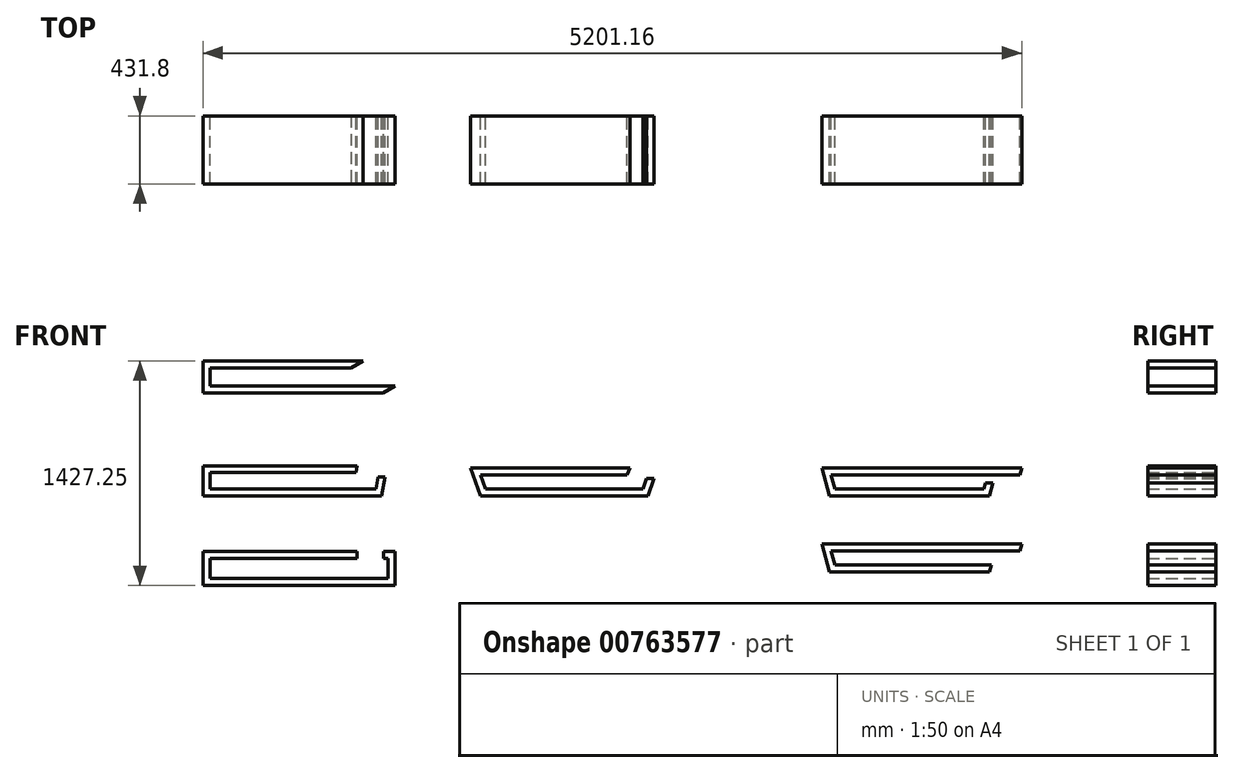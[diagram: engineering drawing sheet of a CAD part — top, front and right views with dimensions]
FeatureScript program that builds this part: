
annotation { "Feature Type Name" : "Feature", "Feature Type Description" : "" }
export const myFeature = defineFeature(function(context is Context, id is Id, definition is map)
    precondition{}
    {
        {
            var Q0;
            Q0=qCreatedBy(makeId("Front.planeOp"),FACE);
            var sketch = newSketch(context, id + "F0", { "sketchPlane" : qUnion([Q0])});
            skLineSegment(sketch, "E0", {"start": v(1016, 203.2) * mm, "end": v(0, 203.2) * mm});
            skLineSegment(sketch, "E1", {"start": v(0, 203.2) * mm, "end": v(0, 0) * mm});
            skLineSegment(sketch, "E2", {"start": v(0, 0) * mm, "end": v(1219.2, 0) * mm});
            skLineSegment(sketch, "E3", {"start": v(1219.2, 0) * mm, "end": v(1219.2, 44.45) * mm});
            skLineSegment(sketch, "E4", {"start": v(1219.2, 44.45) * mm, "end": v(44.45, 44.45) * mm});
            skLineSegment(sketch, "E5", {"start": v(44.45, 44.45) * mm, "end": v(44.45, 158.75) * mm});
            skLineSegment(sketch, "E6", {"start": v(44.45, 158.75) * mm, "end": v(1016, 158.75) * mm});
            skLineSegment(sketch, "E7", {"start": v(1016, 158.75) * mm, "end": v(1016, 203.2) * mm});
            skLineSegment(sketch, "E8", {"start": v(980.24, -462.8) * mm, "end": v(0, -462.8) * mm});
            skLineSegment(sketch, "E9", {"start": v(0, -462.8) * mm, "end": v(0, -653.3) * mm});
            skLineSegment(sketch, "E10", {"start": v(0, -653.3) * mm, "end": v(1136.08, -653.3) * mm});
            skLineSegment(sketch, "E11", {"start": v(1136.08, -653.3) * mm, "end": v(1157.46, -532.09) * mm});
            skLineSegment(sketch, "E12", {"start": v(1157.46, -532.09) * mm, "end": v(1112.32, -532.09) * mm});
            skLineSegment(sketch, "E13", {"start": v(1112.32, -532.09) * mm, "end": v(1098.78, -608.85) * mm});
            skLineSegment(sketch, "E14", {"start": v(1098.78, -608.85) * mm, "end": v(44.45, -608.85) * mm});
            skLineSegment(sketch, "E15", {"start": v(44.45, -608.85) * mm, "end": v(44.45, -506.58) * mm});
            skLineSegment(sketch, "E16", {"start": v(44.45, -506.58) * mm, "end": v(972.52, -506.58) * mm});
            skLineSegment(sketch, "E17", {"start": v(972.52, -506.58) * mm, "end": v(980.24, -462.8) * mm});
            skLineSegment(sketch, "E18", {"start": v(980.24, -1007.28) * mm, "end": v(0, -1007.28) * mm});
            skLineSegment(sketch, "E19", {"start": v(0, -1007.28) * mm, "end": v(0, -1224.05) * mm});
            skLineSegment(sketch, "E20", {"start": v(0, -1224.05) * mm, "end": v(1219.2, -1224.05) * mm});
            skLineSegment(sketch, "E21", {"start": v(1219.2, -1224.05) * mm, "end": v(1219.2, -1007.28) * mm});
            skLineSegment(sketch, "E22", {"start": v(1219.2, -1007.28) * mm, "end": v(1146.26, -1007.28) * mm});
            skLineSegment(sketch, "E23", {"start": v(1146.26, -1007.28) * mm, "end": v(1146.26, -1051.73) * mm});
            skLineSegment(sketch, "E24", {"start": v(1146.26, -1051.73) * mm, "end": v(1174.75, -1051.73) * mm});
            skLineSegment(sketch, "E25", {"start": v(1174.75, -1051.73) * mm, "end": v(1174.75, -1179.6) * mm});
            skLineSegment(sketch, "E26", {"start": v(1174.75, -1179.6) * mm, "end": v(44.45, -1179.6) * mm});
            skLineSegment(sketch, "E27", {"start": v(44.45, -1179.6) * mm, "end": v(44.45, -1051.73) * mm});
            skLineSegment(sketch, "E28", {"start": v(44.45, -1051.73) * mm, "end": v(980.24, -1051.73) * mm});
            skLineSegment(sketch, "E29", {"start": v(980.24, -1051.73) * mm, "end": v(980.24, -1007.28) * mm});
            skLineSegment(sketch, "E30", {"start": v(2711.3, -475.5) * mm, "end": v(1698.34, -475.5) * mm});
            skLineSegment(sketch, "E31", {"start": v(1698.34, -475.5) * mm, "end": v(1763.05, -653.3) * mm});
            skLineSegment(sketch, "E32", {"start": v(1763.05, -653.3) * mm, "end": v(2826.15, -653.3) * mm});
            skLineSegment(sketch, "E33", {"start": v(2826.15, -653.3) * mm, "end": v(2866.22, -543.22) * mm});
            skLineSegment(sketch, "E34", {"start": v(2866.22, -543.22) * mm, "end": v(2818.91, -543.22) * mm});
            skLineSegment(sketch, "E35", {"start": v(2818.91, -543.22) * mm, "end": v(2795.03, -608.85) * mm});
            skLineSegment(sketch, "E36", {"start": v(2795.03, -608.85) * mm, "end": v(1794.17, -608.85) * mm});
            skLineSegment(sketch, "E37", {"start": v(1794.17, -608.85) * mm, "end": v(1761.82, -519.95) * mm});
            skLineSegment(sketch, "E38", {"start": v(1761.82, -519.95) * mm, "end": v(2695.12, -519.95) * mm});
            skLineSegment(sketch, "E39", {"start": v(2695.12, -519.95) * mm, "end": v(2711.3, -475.5) * mm});
            skLineSegment(sketch, "E40", {"start": v(5201.16, -475.5) * mm, "end": v(3931.16, -475.5) * mm});
            skLineSegment(sketch, "E41", {"start": v(3931.16, -475.5) * mm, "end": v(3978.8, -653.3) * mm});
            skLineSegment(sketch, "E42", {"start": v(3978.8, -653.3) * mm, "end": v(4994.8, -653.3) * mm});
            skLineSegment(sketch, "E43", {"start": v(4994.8, -653.3) * mm, "end": v(5016.92, -570.75) * mm});
            skLineSegment(sketch, "E44", {"start": v(5016.92, -570.75) * mm, "end": v(4970.9, -570.75) * mm});
            skLineSegment(sketch, "E45", {"start": v(4970.9, -570.75) * mm, "end": v(4960.7, -608.85) * mm});
            skLineSegment(sketch, "E46", {"start": v(4960.7, -608.85) * mm, "end": v(4012.91, -608.85) * mm});
            skLineSegment(sketch, "E47", {"start": v(4012.91, -608.85) * mm, "end": v(3989.1, -519.95) * mm});
            skLineSegment(sketch, "E48", {"start": v(3989.1, -519.95) * mm, "end": v(5189.25, -519.95) * mm});
            skLineSegment(sketch, "E49", {"start": v(5189.25, -519.95) * mm, "end": v(5201.16, -475.5) * mm});
            skLineSegment(sketch, "E50", {"start": v(3989.1, -519.95) * mm, "end": v(3931.16, -475.5) * mm});
            skLineSegment(sketch, "E51", {"start": v(4012.91, -608.85) * mm, "end": v(3978.8, -653.3) * mm});
            skLineSegment(sketch, "E52", {"start": v(4960.7, -608.85) * mm, "end": v(4994.8, -653.3) * mm});
            skLineSegment(sketch, "E53", {"start": v(5201.16, -959.68) * mm, "end": v(3931.16, -959.68) * mm});
            skLineSegment(sketch, "E54", {"start": v(3931.16, -959.68) * mm, "end": v(3978.8, -1137.48) * mm});
            skLineSegment(sketch, "E55", {"start": v(3978.8, -1137.48) * mm, "end": v(4994.8, -1137.48) * mm});
            skLineSegment(sketch, "E56", {"start": v(5006.71, -1093.03) * mm, "end": v(4012.91, -1093.03) * mm});
            skLineSegment(sketch, "E57", {"start": v(4012.91, -1093.03) * mm, "end": v(3989.1, -1004.13) * mm});
            skLineSegment(sketch, "E58", {"start": v(3989.1, -1004.13) * mm, "end": v(5189.25, -1004.13) * mm});
            skLineSegment(sketch, "E59", {"start": v(5189.25, -1004.13) * mm, "end": v(5201.16, -959.68) * mm});
            skLineSegment(sketch, "E60", {"start": v(3989.1, -1004.13) * mm, "end": v(3931.16, -959.68) * mm});
            skLineSegment(sketch, "E61", {"start": v(4012.91, -1093.03) * mm, "end": v(3978.8, -1137.48) * mm});
            skLineSegment(sketch, "E62", {"start": v(5006.71, -1093.03) * mm, "end": v(4994.8, -1137.48) * mm});
            skSolve(sketch);
        }
        {
            var Q0;
            Q0 = qSketchRegion(id + "F0", true);
            extrude(context, id + "F1", {"entities" : qUnion([Q0]), "depth" : 431.8 * mm, "offsetDistance" : 25.4 * mm});
        }
        {
            var Q0;
            Q0=makeQuery(id+"F1.opExtrude","SWEPT_EDGE",EDGE,{"disambiguationData":[OSD([sQuery(id+"F0.wireOp",EDGE,"E2"),sQuery(id+"F0.wireOp",EDGE,"E3")])]});
            var Q1;
            Q1=makeQuery(id+"F1.opExtrude","SWEPT_EDGE",EDGE,{"disambiguationData":[OSD([sQuery(id+"F0.wireOp",EDGE,"E6"),sQuery(id+"F0.wireOp",EDGE,"E7")])]});
            chamfer(context, id + "F2", {"entities" : qUnion([Q0, Q1]), "chamferType" : ChamferType.OFFSET_ANGLE, "width" : 43.18 * mm, "oppositeDirection" : false, "angle" : 60 * degree, "tangentPropagation" : true});
        }
    });
